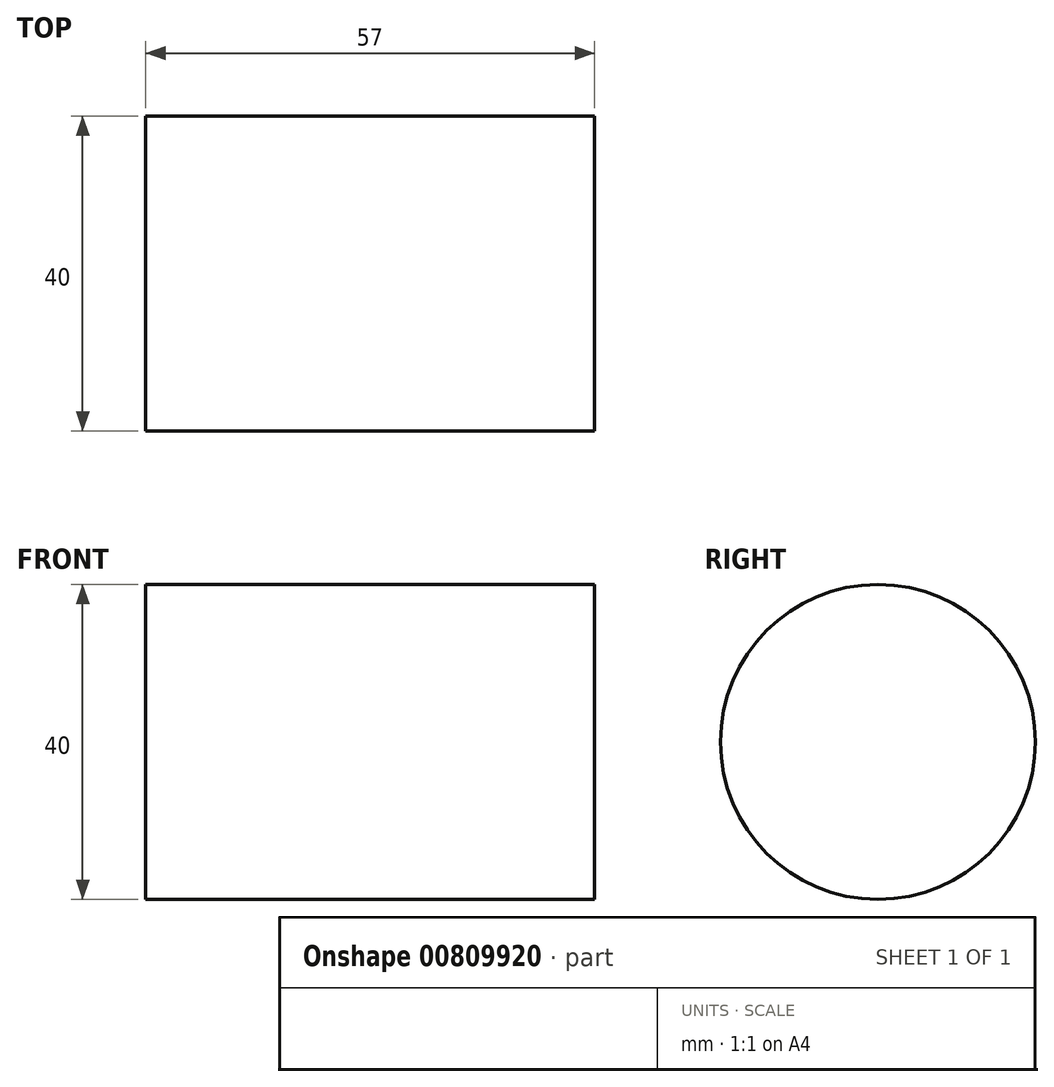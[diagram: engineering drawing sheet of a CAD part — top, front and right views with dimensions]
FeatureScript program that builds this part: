
annotation { "Feature Type Name" : "Feature", "Feature Type Description" : "" }
export const myFeature = defineFeature(function(context is Context, id is Id, definition is map)
    precondition{}
    {
        {
            var Q0;
            Q0=qCreatedBy(makeId("Right.planeOp"),FACE);
            var sketch = newSketch(context, id + "F0", { "sketchPlane" : qUnion([Q0])});
            skCircle(sketch, "E0", {"center": v(0, 0) * mm, "radius": 20 * mm});
            skSolve(sketch);
        }
        {
            var Q0;
            Q0=makeQuery(id+"F0.imprint","IMPRINT",FACE,{"disambiguationData":[TD([[makeQuery(id+"F0.imprint","IMPRINT",EDGE,{"derivedFrom":sQuery(id+"F0.wireOp",EDGE,"E0")}),1.0]])]});
            extrude(context, id + "F1", {"entities" : qUnion([Q0]), "depth" : 57 * mm, "offsetDistance" : 25 * mm});
        }
    });
